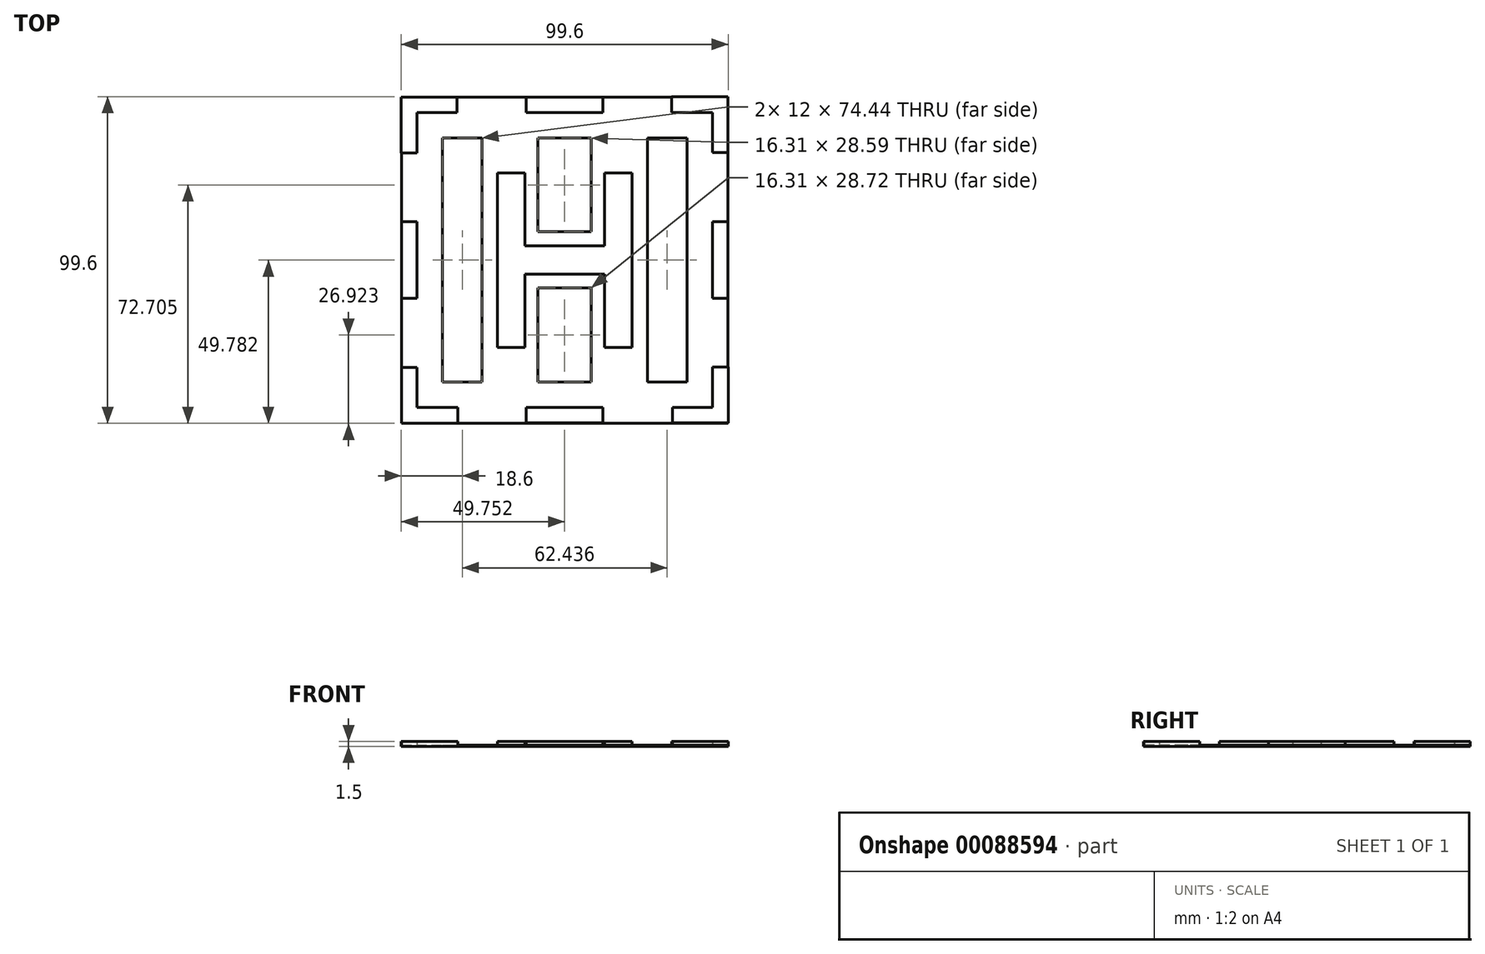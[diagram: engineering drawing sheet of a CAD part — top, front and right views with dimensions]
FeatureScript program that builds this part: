
annotation { "Feature Type Name" : "Feature", "Feature Type Description" : "" }
export const myFeature = defineFeature(function(context is Context, id is Id, definition is map)
    precondition{}
    {
        {
            var Q0;
            Q0=qCreatedBy(makeId("Top.planeOp"),FACE);
            var sketch = newSketch(context, id + "F0", { "sketchPlane" : qUnion([Q0])});
            skLineSegment(sketch, "E0", {"start": v(-12.1, 26.6) * mm, "end": v(-12.1, 4.3) * mm});
            skLineSegment(sketch, "E1", {"start": v(-12.1, 4.3) * mm, "end": v(0, 4.3) * mm});
            skLineSegment(sketch, "E2", {"start": v(-12.1, 26.6) * mm, "end": v(-20.5, 26.6) * mm});
            skLineSegment(sketch, "E3", {"start": v(-20.5, 26.6) * mm, "end": v(-20.5, -26.6) * mm});
            skLineSegment(sketch, "E4", {"start": v(-20.5, -26.6) * mm, "end": v(-12.1, -26.6) * mm});
            skLineSegment(sketch, "E5", {"start": v(-12.1, -26.6) * mm, "end": v(-12.1, -4.3) * mm});
            skLineSegment(sketch, "E6", {"start": v(-12.1, -4.3) * mm, "end": v(0, -4.3) * mm});
            skLineSegment(sketch, "E7.MirrorCS", {"start": v(12.1, 4.3) * mm, "end": v(0, 4.3) * mm});
            skLineSegment(sketch, "E8.MirrorCS", {"start": v(12.1, 26.6) * mm, "end": v(12.1, 4.3) * mm});
            skLineSegment(sketch, "E9.MirrorCS", {"start": v(12.1, 26.6) * mm, "end": v(20.5, 26.6) * mm});
            skLineSegment(sketch, "E10.MirrorCS", {"start": v(20.5, 26.6) * mm, "end": v(20.5, -26.6) * mm});
            skLineSegment(sketch, "E11.MirrorCS", {"start": v(20.5, -26.6) * mm, "end": v(12.1, -26.6) * mm});
            skLineSegment(sketch, "E12.MirrorCS", {"start": v(12.1, -4.3) * mm, "end": v(0, -4.3) * mm});
            skLineSegment(sketch, "E13.MirrorCS", {"start": v(12.1, -26.6) * mm, "end": v(12.1, -4.3) * mm});
            skLineSegment(sketch, "E14", {"start": v(-11.7, 45) * mm, "end": v(0, 45) * mm});
            skLineSegment(sketch, "E15", {"start": v(-11.7, 45) * mm, "end": v(-11.7, 49.7) * mm});
            skLineSegment(sketch, "E16", {"start": v(-32.8, 49.7) * mm, "end": v(-32.8, 45) * mm});
            skLineSegment(sketch, "E17", {"start": v(-32.8, 45) * mm, "end": v(-45, 45) * mm});
            skLineSegment(sketch, "E18", {"start": v(-45, 45) * mm, "end": v(-45, 32.7) * mm});
            skLineSegment(sketch, "E19", {"start": v(-49.7, 11.7) * mm, "end": v(-45, 11.7) * mm});
            skLineSegment(sketch, "E20", {"start": v(-45, 11.7) * mm, "end": v(-45, 0) * mm});
            skPoint(sketch, "E21.center", {"position": v(0, 0) * mm});
            skLineSegment(sketch, "E22", {"start": v(-32.8, 49.7) * mm, "end": v(-49.8, 49.7) * mm});
            skLineSegment(sketch, "E23", {"start": v(-49.8, 49.7) * mm, "end": v(-49.8, 32.7) * mm});
            skLineSegment(sketch, "E24", {"start": v(-49.7, 11.7) * mm, "end": v(-49.7, 0) * mm});
            skLineSegment(sketch, "E25", {"start": v(-11.7, 49.7) * mm, "end": v(0, 49.7) * mm});
            skLineSegment(sketch, "E26.1.0", {"start": v(-45, -11.7) * mm, "end": v(-45, 0) * mm});
            skLineSegment(sketch, "E26.1.1", {"start": v(-45, -45) * mm, "end": v(-32.6, -45) * mm});
            skLineSegment(sketch, "E26.1.2", {"start": v(-49.7, -32.8) * mm, "end": v(-49.7, -49.8) * mm});
            skLineSegment(sketch, "E26.1.3", {"start": v(-49.7, -32.8) * mm, "end": v(-45, -32.8) * mm});
            skLineSegment(sketch, "E26.1.4", {"start": v(-45, -32.8) * mm, "end": v(-45, -45) * mm});
            skLineSegment(sketch, "E26.1.5", {"start": v(-32.6, -45) * mm, "end": v(-32.6, -49.8) * mm});
            skLineSegment(sketch, "E26.1.6", {"start": v(-49.7, -49.8) * mm, "end": v(-32.6, -49.8) * mm});
            skLineSegment(sketch, "E26.1.7", {"start": v(-49.7, -11.7) * mm, "end": v(-49.7, 0) * mm});
            skLineSegment(sketch, "E26.1.8", {"start": v(-45, -11.7) * mm, "end": v(-49.7, -11.7) * mm});
            skLineSegment(sketch, "E26.1.9", {"start": v(-11.7, -49.7) * mm, "end": v(-11.7, -45) * mm});
            skLineSegment(sketch, "E26.1.10", {"start": v(-11.7, -45) * mm, "end": v(0, -45) * mm});
            skLineSegment(sketch, "E26.1.11", {"start": v(-11.7, -49.7) * mm, "end": v(0, -49.7) * mm});
            skLineSegment(sketch, "E26.2.0", {"start": v(11.7, -45) * mm, "end": v(0, -45) * mm});
            skLineSegment(sketch, "E26.2.1", {"start": v(45, -45) * mm, "end": v(45, -32.6) * mm});
            skLineSegment(sketch, "E26.2.2", {"start": v(32.8, -49.7) * mm, "end": v(49.8, -49.7) * mm});
            skLineSegment(sketch, "E26.2.3", {"start": v(32.8, -49.7) * mm, "end": v(32.8, -45) * mm});
            skLineSegment(sketch, "E26.2.4", {"start": v(32.8, -45) * mm, "end": v(45, -45) * mm});
            skLineSegment(sketch, "E26.2.5", {"start": v(45, -32.6) * mm, "end": v(49.8, -32.6) * mm});
            skLineSegment(sketch, "E26.2.6", {"start": v(49.8, -49.7) * mm, "end": v(49.8, -32.6) * mm});
            skLineSegment(sketch, "E26.2.7", {"start": v(11.7, -49.7) * mm, "end": v(0, -49.7) * mm});
            skLineSegment(sketch, "E26.2.8", {"start": v(11.7, -45) * mm, "end": v(11.7, -49.7) * mm});
            skLineSegment(sketch, "E26.2.9", {"start": v(49.7, -11.7) * mm, "end": v(45, -11.7) * mm});
            skLineSegment(sketch, "E26.2.10", {"start": v(45, -11.7) * mm, "end": v(45, 0) * mm});
            skLineSegment(sketch, "E26.2.11", {"start": v(49.7, -11.7) * mm, "end": v(49.7, 0) * mm});
            skLineSegment(sketch, "E26.3.0", {"start": v(45, 11.7) * mm, "end": v(45, 0) * mm});
            skLineSegment(sketch, "E26.3.1", {"start": v(45, 45) * mm, "end": v(32.6, 45) * mm});
            skLineSegment(sketch, "E26.3.2", {"start": v(49.7, 32.8) * mm, "end": v(49.7, 49.8) * mm});
            skLineSegment(sketch, "E26.3.3", {"start": v(49.7, 32.8) * mm, "end": v(45, 32.8) * mm});
            skLineSegment(sketch, "E26.3.4", {"start": v(45, 32.8) * mm, "end": v(45, 45) * mm});
            skLineSegment(sketch, "E26.3.5", {"start": v(32.6, 45) * mm, "end": v(32.6, 49.8) * mm});
            skLineSegment(sketch, "E26.3.6", {"start": v(49.7, 49.8) * mm, "end": v(32.6, 49.8) * mm});
            skLineSegment(sketch, "E26.3.7", {"start": v(49.7, 11.7) * mm, "end": v(49.7, 0) * mm});
            skLineSegment(sketch, "E26.3.8", {"start": v(45, 11.7) * mm, "end": v(49.7, 11.7) * mm});
            skLineSegment(sketch, "E26.3.9", {"start": v(11.7, 49.7) * mm, "end": v(11.7, 45) * mm});
            skLineSegment(sketch, "E26.3.10", {"start": v(11.7, 45) * mm, "end": v(0, 45) * mm});
            skLineSegment(sketch, "E26.3.11", {"start": v(11.7, 49.7) * mm, "end": v(0, 49.7) * mm});
            skLineSegment(sketch, "E27", {"start": v(-49.8, 32.7) * mm, "end": v(-45, 32.7) * mm});
            skPoint(sketch, "E28.orphan", {"position": v(-45, 32.6) * mm});
            skPoint(sketch, "E29.orphan", {"position": v(-49.8, 32.6) * mm});
            skSolve(sketch);
        }
        {
            var Q0;
            Q0 = qSketchRegion(id + "F0", true);
            extrude(context, id + "F1", {"entities" : qUnion([Q0]), "depth" : 1.5 * mm});
        }
        {
            var Q0;
            Q0=qCreatedBy(makeId("Top.planeOp"),FACE);
            var sketch = newSketch(context, id + "F2", { "sketchPlane" : qUnion([Q0])});
            skLineSegment(sketch, "E30.bottom", {"start": v(-49.7, 49.7) * mm, "end": v(49.74, 49.7) * mm});
            skLineSegment(sketch, "E30.top", {"start": v(-49.7, -49.74) * mm, "end": v(49.74, -49.74) * mm});
            skLineSegment(sketch, "E30.left", {"start": v(-49.7, 49.7) * mm, "end": v(-49.7, -49.74) * mm});
            skLineSegment(sketch, "E30.right", {"start": v(49.74, 49.7) * mm, "end": v(49.74, -49.74) * mm});
            skLineSegment(sketch, "E31.bottom", {"start": v(-37.2, 37.2) * mm, "end": v(-25.2, 37.2) * mm});
            skLineSegment(sketch, "E31.top", {"start": v(-37.2, -37.24) * mm, "end": v(-25.2, -37.24) * mm});
            skLineSegment(sketch, "E31.left", {"start": v(-37.2, 37.2) * mm, "end": v(-37.2, -37.24) * mm});
            skLineSegment(sketch, "E31.right", {"start": v(-25.2, 37.2) * mm, "end": v(-25.2, -37.24) * mm});
            skLineSegment(sketch, "E32.bottom", {"start": v(25.24, -37.24) * mm, "end": v(37.24, -37.24) * mm});
            skLineSegment(sketch, "E32.top", {"start": v(25.24, 37.2) * mm, "end": v(37.24, 37.2) * mm});
            skLineSegment(sketch, "E32.left", {"start": v(25.24, -37.24) * mm, "end": v(25.24, 37.2) * mm});
            skLineSegment(sketch, "E32.right", {"start": v(37.24, -37.24) * mm, "end": v(37.24, 37.2) * mm});
            skLineSegment(sketch, "E33.bottom", {"start": v(-8.2, 37.2) * mm, "end": v(8.1, 37.2) * mm});
            skLineSegment(sketch, "E33.top", {"start": v(-8.2, -37.24) * mm, "end": v(8.1, -37.24) * mm});
            skLineSegment(sketch, "E33.left", {"start": v(-8.2, 37.2) * mm, "end": v(-8.2, 8.6) * mm});
            skLineSegment(sketch, "E33.right", {"start": v(8.1, 37.2) * mm, "end": v(8.1, 8.6) * mm});
            skLineSegment(sketch, "E34", {"start": v(-8.2, 8.6) * mm, "end": v(8.1, 8.6) * mm});
            skPoint(sketch, "E34.endSnap0", {"position": v(8.1, -0.02) * mm});
            skLineSegment(sketch, "E35", {"start": v(-8.2, -8.52) * mm, "end": v(8.1, -8.52) * mm});
            skLineSegment(sketch, "E36.trimOffspring", {"start": v(-8.2, -8.52) * mm, "end": v(-8.2, -37.24) * mm});
            skLineSegment(sketch, "E37.trimOffspring", {"start": v(8.1, -8.52) * mm, "end": v(8.1, -37.24) * mm});
            skSolve(sketch);
        }
        {
            var Q0;
            Q0 = qSketchRegion(id + "F2", true);
            extrude(context, id + "F3", {"entities" : qUnion([Q0]), "depth" : .3 * mm});
        }
    });
